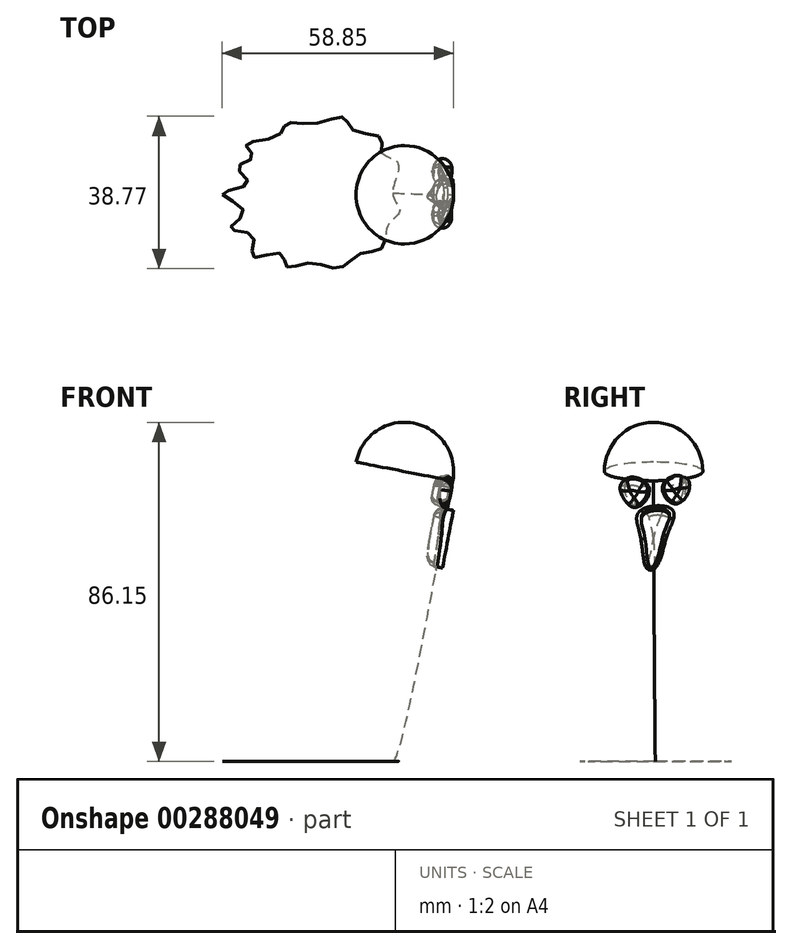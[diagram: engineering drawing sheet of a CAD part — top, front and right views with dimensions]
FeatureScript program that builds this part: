
annotation { "Feature Type Name" : "Feature", "Feature Type Description" : "" }
export const myFeature = defineFeature(function(context is Context, id is Id, definition is map)
    precondition{}
    {
        {
            var Q0;
            Q0=qCreatedBy(makeId("Top.planeOp"),FACE);
            var sketch = newSketch(context, id + "F0", { "sketchPlane" : qUnion([Q0])});
            skFitSpline(sketch, "E0", {"points": [v(-8.9, 18.07) * mm, v(-1.27, 19.7) * mm, v(1.1, 16.44) * mm, v(8.24, 14.44) * mm, v(8.36, 10.81) * mm, v(12.49, 8.06) * mm, v(11.24, 0.32) * mm, v(13, -4.2) * mm, v(10.11, -7.57) * mm, v(8.49, -13.45) * mm, v(2.73, -15.07) * mm, v(-2.27, -18.58) * mm, v(-10.02, -17.33) * mm, v(-15.78, -18.2) * mm, v(-17.28, -14.95) * mm, v(-24.4, -15.7) * mm, v(-24.28, -10.45) * mm, v(-30.03, -8.57) * mm, v(-26.66, -4.2) * mm, v(-32.16, 0.32) * mm, v(-25.53, 2.94) * mm, v(-28.16, 6.94) * mm, v(-24.28, 9.56) * mm, v(-26.03, 12.7) * mm, v(-18.03, 14.94) * mm, v(-15.78, 18.07) * mm, v(-8.9, 18.07) * mm]});
            skSolve(sketch);
        }
        {
            var Q0;
            Q0=qCreatedBy(makeId("Front.planeOp"),FACE);
            var sketch = newSketch(context, id + "F1", { "sketchPlane" : qUnion([Q0])});
            skLineSegment(sketch, "E1", {"start": v(0, 0) * mm, "end": v(14.18, 73.65) * mm});
            skSolve(sketch);
        }
        {
            var Q0;
            Q0=sQuery(id+"F1.wireOp",VERTEX,"E1.end");
            var Q1;
            Q1=sQuery(id+"F1.wireOp",EDGE,"E1");
            cPlane(context, id + "F2", {"entities" : qUnion([Q0, Q1]), "cplaneType" : CPlaneType.LINE_POINT, "offset" : 25 * mm, "width" : 150 * mm, "height" : 150 * mm});
        }
        {
            var Q0;
            Q0=qCreatedBy(id+"F2.planeOp",FACE);
            var sketch = newSketch(context, id + "F3", { "sketchPlane" : qUnion([Q0])});
            skCircle(sketch, "E2", {"center": v(0, 0) * mm, "radius": 12.5 * mm});
            skLineSegment(sketch, "E3", {"start": v(-12.5, 0) * mm, "end": v(12.5, 0) * mm});
            skSolve(sketch);
        }
        {
            var Q0;
            {var subQ0=sQuery(id+"F3.wireOp",EDGE,"E3");Q0=makeQuery(id+"F3.imprint","IMPRINT",FACE,{"disambiguationData":[TD([[makeQuery(id+"F3.imprint","IMPRINT",EDGE,{"derivedFrom":subQ0}),1.0]])]});}
            var Q1;
            Q1=sQuery(id+"F3.wireOp",EDGE,"E3");
            revolve(context, id + "F4", {"entities" : qUnion([Q0]), "axis" : qUnion([Q1]), "revolveType" : RevolveType.ONE_DIRECTION, "angle" : 180 * degree});
        }
        {
            var Q1;
            Q1=makeQuery(id+"F0.imprint","IMPRINT",FACE,{"disambiguationData":[TD([[makeQuery(id+"F0.imprint","IMPRINT",EDGE,{"derivedFrom":sQuery(id+"F0.wireOp",EDGE,"E0")}),-1.0]])]});
            var Q2;
            Q2=makeQuery(id+"F3.imprint","IMPRINT",FACE,{"disambiguationData":[TD([[makeQuery(id+"F3.imprint","IMPRINT",EDGE,{"derivedFrom":sQuery(id+"F3.wireOp",EDGE,"E2")}),1.0]])]});
            loft(context, id + "F5", {"operationType" : NewBodyOperationType.ADD, "startCondition" : LoftEndDerivativeType.TANGENT_TO_PROFILE, "startMagnitude" : .5, "endCondition" : LoftEndDerivativeType.NORMAL_TO_PROFILE, "endMagnitude" : 1, "sheetProfilesArray" : [{ "sheetProfileEntities" : qUnion([Q1]) }, { "sheetProfileEntities" : qUnion([Q2]) }]});
        }
        {
            var Q0;
            Q0=sQuery(id+"F3.wireOp",VERTEX,"E3.end");
            var Q1;
            Q1=sQuery(id+"F3.wireOp",EDGE,"E3");
            cPlane(context, id + "F6", {"entities" : qUnion([Q0, Q1]), "cplaneType" : CPlaneType.LINE_POINT, "offset" : 25 * mm, "width" : 150 * mm, "height" : 150 * mm});
        }
        {
            var Q0;
            Q0=qCreatedBy(id+"F6.planeOp",FACE);
            var sketch = newSketch(context, id + "F7", { "sketchPlane" : qUnion([Q0])});
            skFitSpline(sketch, "E4", {"points": [v(0.67, 67.63) * mm, v(3.95, 66.51) * mm, v(2.76, 62.2) * mm, v(0.57, 54.27) * mm, v(-0.92, 52.8) * mm, v(-2.26, 60.92) * mm, v(-2.92, 66.01) * mm, v(0.67, 67.63) * mm]});
            skFitSpline(sketch, "E5", {"points": [v(8.77, 75.07) * mm, v(2.8, 73.8) * mm, v(6.23, 69.1) * mm, v(8.77, 75.07) * mm]});
            skFitSpline(sketch, "E6", {"points": [v(-1.77, 73.6) * mm, v(-8.18, 74.16) * mm, v(-5.05, 68.39) * mm, v(-1.77, 73.6) * mm]});
            skSolve(sketch);
        }
        {
            var Q0;
            Q0=makeQuery(id+"F7.imprint","IMPRINT",FACE,{"disambiguationData":[TD([[makeQuery(id+"F7.imprint","IMPRINT",EDGE,{"derivedFrom":sQuery(id+"F7.wireOp",EDGE,"E6")}),1.0]])]});
            var Q1;
            Q1=makeQuery(id+"F7.imprint","IMPRINT",FACE,{"disambiguationData":[TD([[makeQuery(id+"F7.imprint","IMPRINT",EDGE,{"derivedFrom":sQuery(id+"F7.wireOp",EDGE,"E5")}),1.0]])]});
            var Q2;
            Q2=makeQuery(id+"F7.imprint","IMPRINT",FACE,{"disambiguationData":[TD([[makeQuery(id+"F7.imprint","IMPRINT",EDGE,{"derivedFrom":sQuery(id+"F7.wireOp",EDGE,"E4")}),-1.0]])]});
            extrude(context, id + "F8", {"entities" : qUnion([Q0, Q1, Q2]), "oppositeDirection" : true, "depth" : 3 * mm, "hasSecondDirection" : true, "secondDirectionOppositeDirection" : false, "secondDirectionDepth" : 1.6 * mm});
        }
        {
            var Q0;
            Q0=makeQuery(id+"F8.opExtrude","CAP_FACE",FACE,{"disambiguationData":[OSD([sQuery(id+"F7.wireOp",EDGE,"E5")])],"isStart":false});
            var Q1;
            Q1=makeQuery(id+"F8.opExtrude","CAP_FACE",FACE,{"disambiguationData":[OSD([sQuery(id+"F7.wireOp",EDGE,"E6")])],"isStart":false});
            var Q2;
            Q2=makeQuery(id+"F8.opExtrude","CAP_FACE",FACE,{"disambiguationData":[OSD([sQuery(id+"F7.wireOp",EDGE,"E4")])],"isStart":false});
            fillet(context, id + "F9", {"entities" : qUnion([Q0, Q1, Q2]), "radius" : 2 * mm, "tangentPropagation" : true, "allowEdgeOverflow" : false});
        }
        {
            var Q0;
            Q0=makeQuery(id+"F8.opExtrude","SWEPT_BODY",BODY,{"disambiguationData":[OSD([sQuery(id+"F7.wireOp",EDGE,"E6")])]});
            var Q1;
            Q1=makeQuery(id+"F8.opExtrude","SWEPT_BODY",BODY,{"disambiguationData":[OSD([sQuery(id+"F7.wireOp",EDGE,"E5")])]});
            var Q2;
            Q2=makeQuery(id+"F8.opExtrude","SWEPT_BODY",BODY,{"disambiguationData":[OSD([sQuery(id+"F7.wireOp",EDGE,"E4")])]});
            var Q3;
            Q3=makeQuery(id+"F4.opRevolve","SWEPT_BODY",BODY,{"disambiguationData":[OSD([sQuery(id+"F3.wireOp",EDGE,"E2"),sQuery(id+"F3.wireOp",EDGE,"E3")])]});
            booleanBodies(context, id + "F10", {"operationType" : BooleanOperationType.SUBTRACTION, "tools" : qUnion([Q0, Q1, Q2]), "targets" : qUnion([Q3]), "keepTools" : true});
        }
        {
            var Q0;
            Q0=makeQuery(id+"F8.opExtrude","CAP_FACE",FACE,{"disambiguationData":[OSD([sQuery(id+"F7.wireOp",EDGE,"E6")])],"isStart":true});
            var Q1;
            Q1=makeQuery(id+"F8.opExtrude","CAP_FACE",FACE,{"disambiguationData":[OSD([sQuery(id+"F7.wireOp",EDGE,"E5")])],"isStart":true});
            fillet(context, id + "F11", {"entities" : qUnion([Q0, Q1]), "radius" : 2.5 * mm, "tangentPropagation" : true, "allowEdgeOverflow" : false});
        }
        {
            var Q0;
            Q0=makeQuery(id+"F10.opBoolean","INTERSECT",EDGE,{"derivedFrom":[makeQuery(id+"F5.opLoft","SWEPT_FACE",FACE,{"disambiguationData":[OSD([sQuery(id+"F0.wireOp",EDGE,"E0"),sQuery(id+"F3.wireOp",EDGE,"E2"),sQuery(id+"F3.wireOp",EDGE,"E3")])]}),makeQuery(id+"F8.opExtrude","SWEPT_FACE",FACE,{"disambiguationData":[OSD([sQuery(id+"F7.wireOp",EDGE,"E4")])]})]});
            fillet(context, id + "F12", {"entities" : qUnion([Q0]), "radius" : 0.9 * mm, "tangentPropagation" : true, "allowEdgeOverflow" : false});
        }
        {
            var Q0;
            Q0=makeQuery(id+"F10.opBoolean","INTERSECT",EDGE,{"derivedFrom":[makeQuery(id+"F5.opLoft","SWEPT_FACE",FACE,{"disambiguationData":[OSD([sQuery(id+"F0.wireOp",EDGE,"E0"),sQuery(id+"F3.wireOp",EDGE,"E2"),sQuery(id+"F3.wireOp",EDGE,"E3")])]}),makeQuery(id+"F9.opFillet","BLEND_FACE",FACE,{"disambiguationData":[OSD([sQuery(id+"F7.wireOp",EDGE,"E6")]),OD(3.0)]})]});
            var Q1;
            Q1=makeQuery(id+"F10.opBoolean","INTERSECT",EDGE,{"derivedFrom":[makeQuery(id+"F5.opLoft","SWEPT_FACE",FACE,{"disambiguationData":[OSD([sQuery(id+"F0.wireOp",EDGE,"E0"),sQuery(id+"F3.wireOp",EDGE,"E2"),sQuery(id+"F3.wireOp",EDGE,"E3")])]}),makeQuery(id+"F9.opFillet","BLEND_FACE",FACE,{"disambiguationData":[OSD([sQuery(id+"F7.wireOp",EDGE,"E6")]),OD(1.0)]})]});
            var Q2;
            Q2=makeQuery(id+"F10.opBoolean","INTERSECT",EDGE,{"derivedFrom":[makeQuery(id+"F5.opLoft","SWEPT_FACE",FACE,{"disambiguationData":[OSD([sQuery(id+"F0.wireOp",EDGE,"E0"),sQuery(id+"F3.wireOp",EDGE,"E2"),sQuery(id+"F3.wireOp",EDGE,"E3")])]}),makeQuery(id+"F9.opFillet","BLEND_FACE",FACE,{"disambiguationData":[OSD([sQuery(id+"F7.wireOp",EDGE,"E6")]),OD(5.0)]})]});
            var Q3;
            Q3=makeQuery(id+"F10.opBoolean","INTERSECT",EDGE,{"derivedFrom":[makeQuery(id+"F4.opRevolve","SWEPT_FACE",FACE,{"disambiguationData":[OSD([sQuery(id+"F3.wireOp",EDGE,"E2")])]}),makeQuery(id+"F9.opFillet","BLEND_FACE",FACE,{"disambiguationData":[OSD([sQuery(id+"F7.wireOp",EDGE,"E6")]),OD(5.0)]})]});
            var Q4;
            Q4=makeQuery(id+"F10.opBoolean","INTERSECT",EDGE,{"derivedFrom":[makeQuery(id+"F4.opRevolve","SWEPT_FACE",FACE,{"disambiguationData":[OSD([sQuery(id+"F3.wireOp",EDGE,"E2")])]}),makeQuery(id+"F8.opExtrude","SWEPT_FACE",FACE,{"disambiguationData":[OSD([sQuery(id+"F7.wireOp",EDGE,"E6")])]})]});
            var Q5;
            Q5=makeQuery(id+"F10.opBoolean","INTERSECT",EDGE,{"derivedFrom":[makeQuery(id+"F5.opLoft","SWEPT_FACE",FACE,{"disambiguationData":[OSD([sQuery(id+"F0.wireOp",EDGE,"E0"),sQuery(id+"F3.wireOp",EDGE,"E2"),sQuery(id+"F3.wireOp",EDGE,"E3")])]}),makeQuery(id+"F8.opExtrude","SWEPT_FACE",FACE,{"disambiguationData":[OSD([sQuery(id+"F7.wireOp",EDGE,"E5")])]})]});
            var Q6;
            Q6=makeQuery(id+"F10.opBoolean","INTERSECT",EDGE,{"derivedFrom":[makeQuery(id+"F4.opRevolve","SWEPT_FACE",FACE,{"disambiguationData":[OSD([sQuery(id+"F3.wireOp",EDGE,"E2")])]}),makeQuery(id+"F8.opExtrude","SWEPT_FACE",FACE,{"disambiguationData":[OSD([sQuery(id+"F7.wireOp",EDGE,"E5")])]})]});
            var Q7;
            Q7=makeQuery(id+"F10.opBoolean","INTERSECT",EDGE,{"derivedFrom":[makeQuery(id+"F4.opRevolve","SWEPT_FACE",FACE,{"disambiguationData":[OSD([sQuery(id+"F3.wireOp",EDGE,"E2")])]}),makeQuery(id+"F9.opFillet","BLEND_FACE",FACE,{"disambiguationData":[OSD([sQuery(id+"F7.wireOp",EDGE,"E5")]),OD(2.0)]})]});
            var Q8;
            Q8=makeQuery(id+"F10.opBoolean","INTERSECT",EDGE,{"derivedFrom":[makeQuery(id+"F5.opLoft","SWEPT_FACE",FACE,{"disambiguationData":[OSD([sQuery(id+"F0.wireOp",EDGE,"E0"),sQuery(id+"F3.wireOp",EDGE,"E2"),sQuery(id+"F3.wireOp",EDGE,"E3")])]}),makeQuery(id+"F9.opFillet","BLEND_FACE",FACE,{"disambiguationData":[OSD([sQuery(id+"F7.wireOp",EDGE,"E5")]),OD(1.0)]})]});
            var Q9;
            Q9=makeQuery(id+"F10.opBoolean","INTERSECT",EDGE,{"derivedFrom":[makeQuery(id+"F5.opLoft","SWEPT_FACE",FACE,{"disambiguationData":[OSD([sQuery(id+"F0.wireOp",EDGE,"E0"),sQuery(id+"F3.wireOp",EDGE,"E2"),sQuery(id+"F3.wireOp",EDGE,"E3")])]}),makeQuery(id+"F9.opFillet","BLEND_FACE",FACE,{"disambiguationData":[OSD([sQuery(id+"F7.wireOp",EDGE,"E5")]),OD(3.0)]})]});
            var Q10;
            Q10=makeQuery(id+"F10.opBoolean","INTERSECT",EDGE,{"derivedFrom":[makeQuery(id+"F5.opLoft","SWEPT_FACE",FACE,{"disambiguationData":[OSD([sQuery(id+"F0.wireOp",EDGE,"E0"),sQuery(id+"F3.wireOp",EDGE,"E2"),sQuery(id+"F3.wireOp",EDGE,"E3")])]}),makeQuery(id+"F9.opFillet","BLEND_FACE",FACE,{"disambiguationData":[OSD([sQuery(id+"F7.wireOp",EDGE,"E5")]),OD(0.0)]})]});
            fillet(context, id + "F13", {"entities" : qUnion([Q0, Q1, Q2, Q3, Q4, Q5, Q6, Q7, Q8, Q9, Q10]), "radius" : .5 * mm, "tangentPropagation" : true, "allowEdgeOverflow" : false});
        }
        {
            var Q0;
            Q0=makeQuery(id+"F8.opExtrude","SWEPT_BODY",BODY,{"disambiguationData":[OSD([sQuery(id+"F7.wireOp",EDGE,"E6")])]});
            var Q1;
            Q1=makeQuery(id+"F8.opExtrude","SWEPT_BODY",BODY,{"disambiguationData":[OSD([sQuery(id+"F7.wireOp",EDGE,"E5")])]});
            transform(context, id + "F14", {"entities" : qUnion([Q0, Q1]), "transformType" : TransformType.TRANSLATION_3D, "dx" : -1.5 * mm, "dy" : 0 * mm, "dz" : 0 * mm, "makeCopy" : false});
        }
    });
